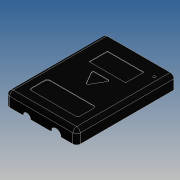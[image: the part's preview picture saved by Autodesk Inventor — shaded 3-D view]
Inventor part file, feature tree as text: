
AUTODESK INVENTOR PART (.ipt)
format: ipt  version: 2019 (Build 230136000, 136)  size: 380,416 bytes
history: native  units: mm
features: fillet x7, sketch x7, extrude x6, mirror x2, shell x1, hole x1
ambient origin geometry x8: Origin, YZ Plane, XZ Plane, XY Plane, X Axis, Y Axis, Z Axis, Center Point
bodies: Solid1 (feature_tree)
feature tree (24):
  extrude  "Extrusion1"  Depth=40.0mm
  shell  "Shell1"  Thickness=11.0mm
  extrude  "Extrusion2"  Depth=1.0mm
  extrude  "Extrusion3"  Depth=10.0mm
  fillet  "Fillet3"  Radius=20.0mm
  mirror  "Mirror1"
  mirror  "Mirror2"
  fillet  "Fillet4"  Radius=0.2mm
  fillet  "Fillet5"  Radius=5.0mm
  fillet  "Fillet6"  Radius=0.2mm
  extrude  "Extrusion4"  Depth=0.2mm
  extrude  "Extrusion6"  Depth=1.0mm
  fillet  "Fillet7"  Radius=3.0mm
  hole  "Hole1"  [1 undecoded]
  extrude  "Extrusion7"  Depth=4.2mm
  fillet  "Fillet8"  Radius=3.2mm
  fillet  "Fillet9"  Radius=10.0mm
  sketch  "Sketch1"  dims[d0=29.0mm d1=40.0mm d2=11.0mm d3=0.0mm]
  sketch  "Sketch2"  dims[d6=2.0mm d7=1.0mm]
  sketch  "Sketch3"  dims[d8=2.0mm d9=0.0mm d10=10.0mm d11=20.0mm d12=0.2mm d13=5.0mm d14=0.2mm]
  sketch  "Sketch4"  dims[d15=0.8mm d16=0.0mm d17=0.2mm]
  sketch  "Sketch5"  dims[d18=1.0mm d19=1.0mm d20=3.0mm]
  sketch  "Sketch6"  dims[d21=3.0mm d22=12.0mm]
  sketch  "Sketch7"  dims[d23=12.0mm d24=4.2mm d25=3.2mm d26=10.0mm d27=0.0mm d32=2.0mm d33=3.0mm d34=10.0mm d35=0.0mm d36=2.0mm d37=6.5mm d38=9.6mm d39=2.0mm d40=6.0mm d41=4.0mm d42=2.0mm d43=90.0deg d44=8.0mm d45=20.594885mm d46=40.0mm d47=15.0mm d48=10.0mm d49=15.0mm d51=5.0mm d52=30.0mm d53=15.0mm d54=5.0mm d55=0.4mm d56=0.0mm d57=2.0mm d58=1.0mm]
note: 1 required parameter value undecoded (feature->parameter linkage not recoverable at this tier; creation-order binding heuristic only, values carry confidence <= 0.55)
